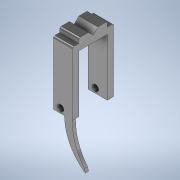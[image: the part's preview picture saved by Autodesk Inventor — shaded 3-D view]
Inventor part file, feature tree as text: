
AUTODESK INVENTOR PART (.ipt)
format: ipt  version: 2021 (Build 250183000, 183)  size: 202,752 bytes
history: native  units: in
note: dims shown in document units (in); Inventor stores cm internally (conversion verified against a paired STEP export)
features: extrude x7, sketch x3, fillet x2, other x1
ambient origin geometry x8: Origin, YZ Plane, XZ Plane, XY Plane, X Axis, Y Axis, Z Axis, Center Point
bodies: Solid1 (feature_tree)
feature tree (13):
  sketch  "Sketch1"  dims[d0=0.1969in d1=0.7874in]
  extrude  "Extrusion1"  Depth=0.7874in
  extrude  "Extrusion2"  Depth=0.5906in
  sketch  "Sketch2"  dims[d2=0.6693in d3=0.5906in]
  extrude  "Extrusion3"  Depth=0.0394in TaperAngle=0.0deg
  extrude  "Extrusion4"  Depth=0.7087in
  extrude  "Extrusion5"  Depth=0.0197in TaperAngle=0.0deg
  extrude  "Extrusion6"  Depth=0.0197in TaperAngle=0.0deg
  fillet  "Arredondamento1"  [1 undecoded]
  fillet  "Arredondamento2"  [1 undecoded]
  extrude  "Extrusão7"  Depth=0.0787in
  sketch  "Esboço3"  dims[d4=0.5118in d5=0.0in d6=0.0394in d7=0.0in d10=0.7087in d11=0.1969in d12=0.0in d13=0.1969in d14=0.0in d15=0.0in d16=0.0in d17=0.0in d18=0.0in d19=0.0787in d20=0.0787in d24=0.0787in d25=0.1772in d26=0.0787in d27=0.0591in d28=0.0591in d29=0.0197in d30=0.0197in d31=0.0394in d32=0.0in d8=0.0197in d9=0.0344in]
  other  "Contorno projetado1"
note: 2 required parameter values undecoded (feature->parameter linkage not recoverable at this tier; creation-order binding heuristic only, values carry confidence <= 0.55)
